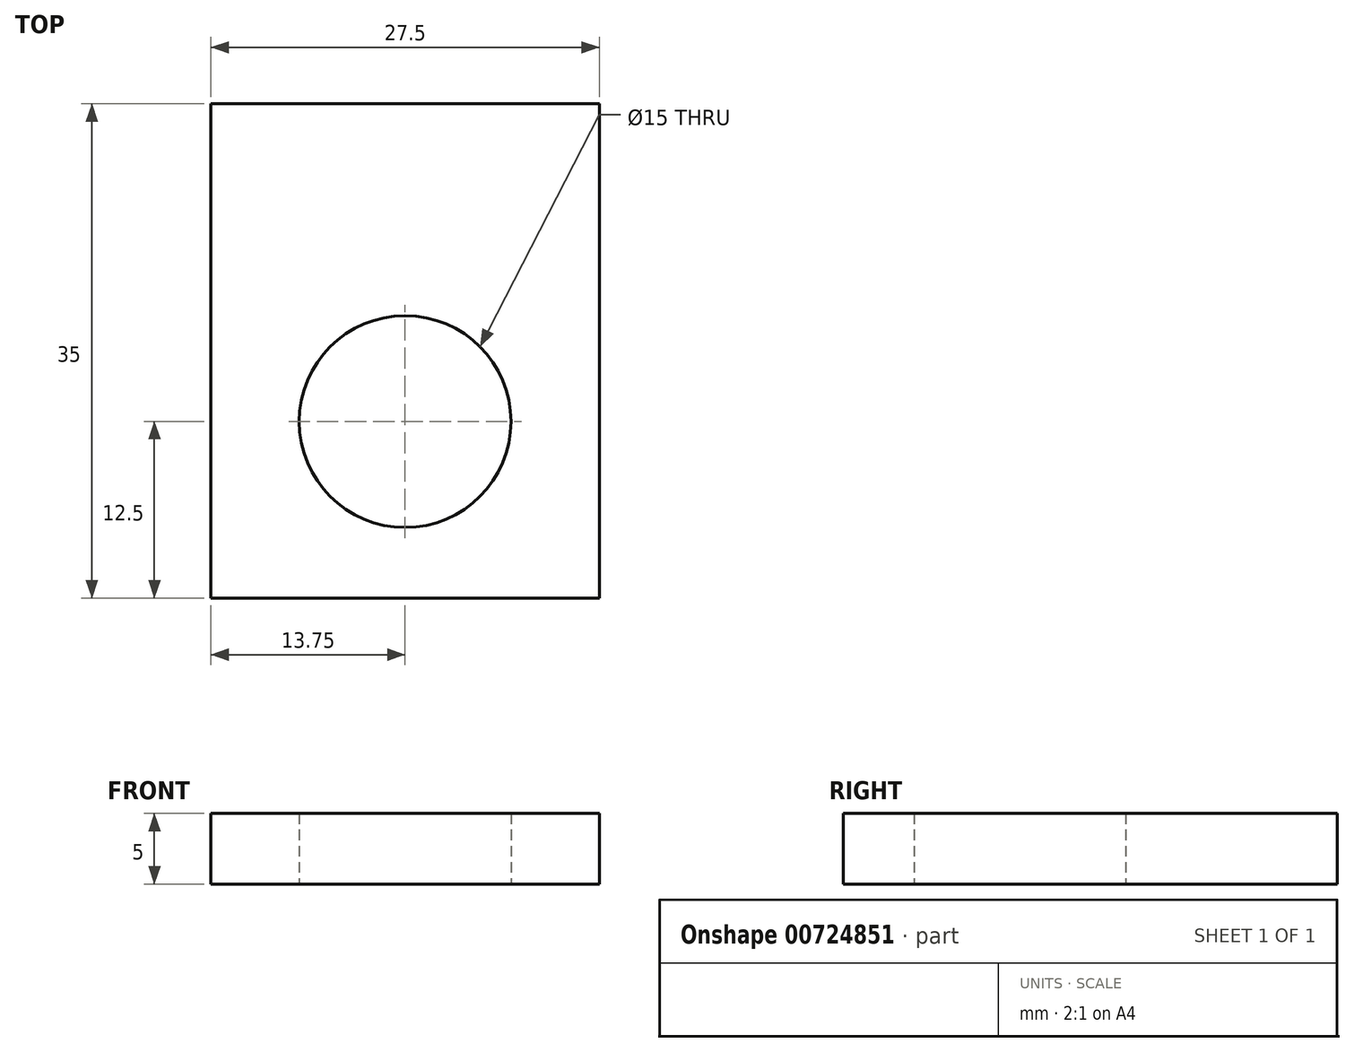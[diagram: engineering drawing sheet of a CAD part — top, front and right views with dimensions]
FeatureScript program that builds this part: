
annotation { "Feature Type Name" : "Feature", "Feature Type Description" : "" }
export const myFeature = defineFeature(function(context is Context, id is Id, definition is map)
    precondition{}
    {
        {
            var Q0;
            Q0=qCreatedBy(makeId("Top.planeOp"),FACE);
            var sketch = newSketch(context, id + "F0", { "sketchPlane" : qUnion([Q0])});
            skLineSegment(sketch, "E0.bottom", {"start": v(0, 0) * mm, "end": v(27.5, 0) * mm});
            skLineSegment(sketch, "E0.top", {"start": v(0, -35) * mm, "end": v(27.5, -35) * mm});
            skLineSegment(sketch, "E0.left", {"start": v(0, 0) * mm, "end": v(0, -35) * mm});
            skLineSegment(sketch, "E0.right", {"start": v(27.5, 0) * mm, "end": v(27.5, -35) * mm});
            skLineSegment(sketch, "E1", {"start": v(13.75, -35) * mm, "end": v(13.75, -22.5) * mm});
            skCircle(sketch, "E2", {"center": v(13.75, -22.5) * mm, "radius": 7.5 * mm});
            skSolve(sketch);
        }
        {
            var Q0;
            Q0 = qSketchRegion(id + "F0", true);
            extrude(context, id + "F1", {"entities" : qUnion([Q0]), "depth" : 5 * mm, "offsetDistance" : 25.4 * mm});
        }
    });
